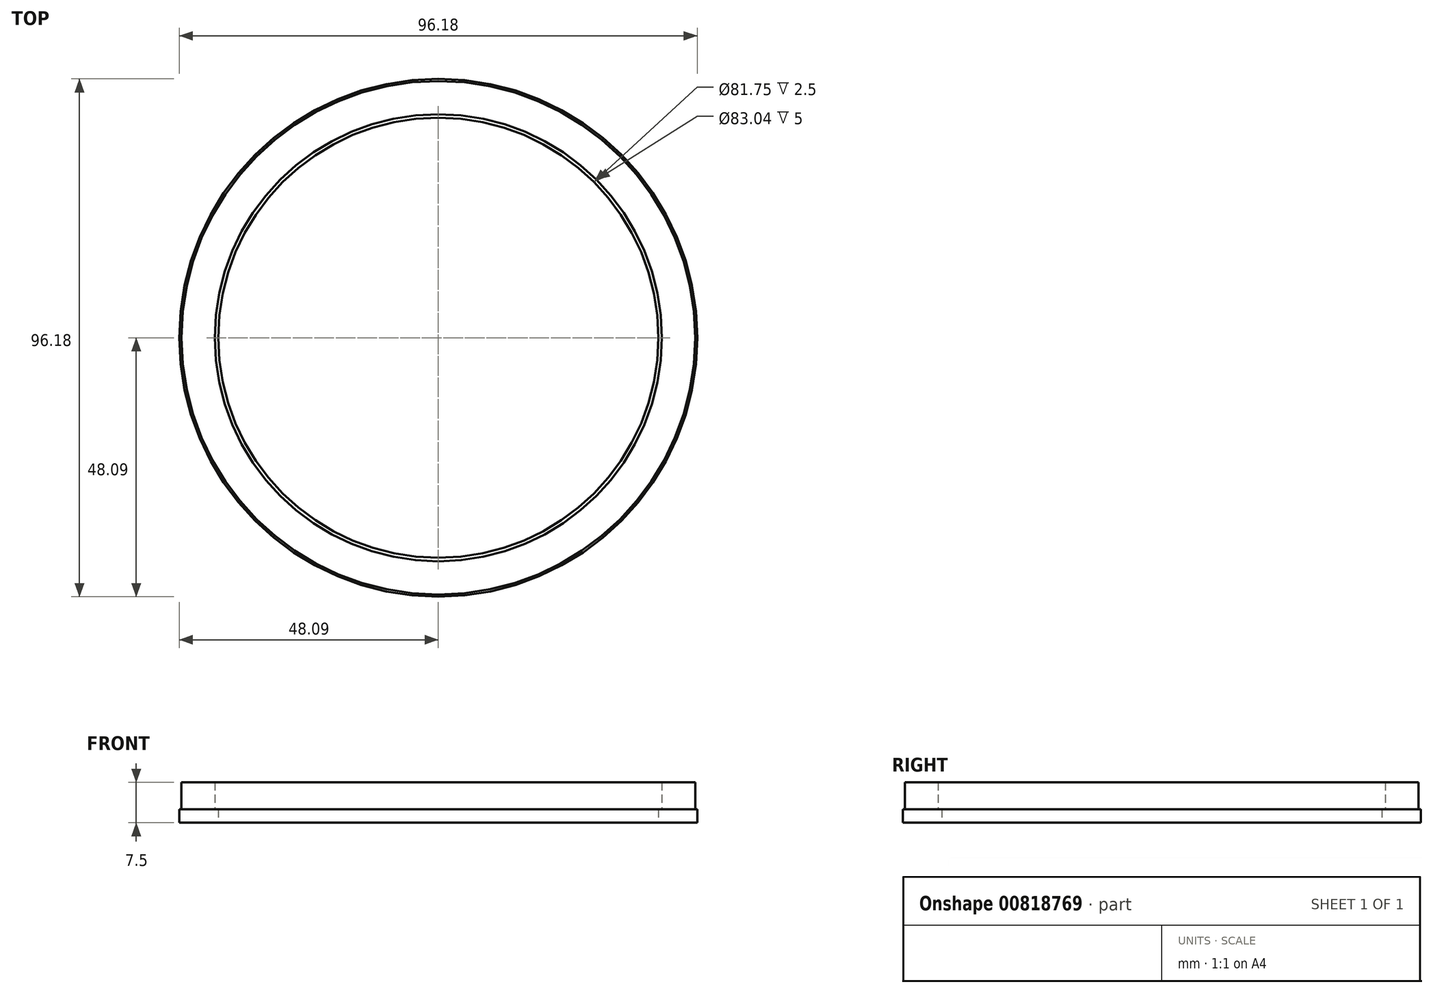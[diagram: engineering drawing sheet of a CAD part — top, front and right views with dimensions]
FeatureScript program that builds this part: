
annotation { "Feature Type Name" : "Feature", "Feature Type Description" : "" }
export const myFeature = defineFeature(function(context is Context, id is Id, definition is map)
    precondition{}
    {
        {
            var Q0;
            Q0=qCreatedBy(makeId("Top.planeOp"),FACE);
            var sketch = newSketch(context, id + "F0", { "sketchPlane" : qUnion([Q0])});
            skCircle(sketch, "E0", {"center": v(0, 0) * mm, "radius": 40.88 * mm});
            skCircle(sketch, "E1", {"center": v(0, 0) * mm, "radius": 48.09 * mm});
            skSolve(sketch);
        }
        {
            var Q0;
            Q0 = qSketchRegion(id + "F0", true);
            extrude(context, id + "F1", {"entities" : qUnion([Q0]), "depth" : 2.5 * mm, "offsetDistance" : 25 * mm});
        }
        {
            var Q0;
            Q0=makeQuery(id+"F1.opExtrude","CAP_FACE",FACE,{"disambiguationData":[OSD([sQuery(id+"F0.wireOp",EDGE,"E0"),sQuery(id+"F0.wireOp",EDGE,"E1")])],"isStart":false});
            var sketch = newSketch(context, id + "F2", { "sketchPlane" : qUnion([Q0])});
            skCircle(sketch, "E2", {"center": v(0, 0) * mm, "radius": 41.52 * mm});
            skCircle(sketch, "E3", {"center": v(0, 0) * mm, "radius": 47.7 * mm});
            skSolve(sketch);
        }
        {
            var Q0;
            Q0=makeQuery(id+"F2.imprint","IMPRINT",FACE,{"disambiguationData":[TD([[makeQuery(id+"F2.imprint","IMPRINT",EDGE,{"derivedFrom":sQuery(id+"F2.wireOp",EDGE,"E2")}),-1.0]])]});
            extrude(context, id + "F3", {"entities" : qUnion([Q0]), "operationType" : NewBodyOperationType.ADD, "depth" : 5 * mm, "offsetDistance" : 25 * mm});
        }
    });
